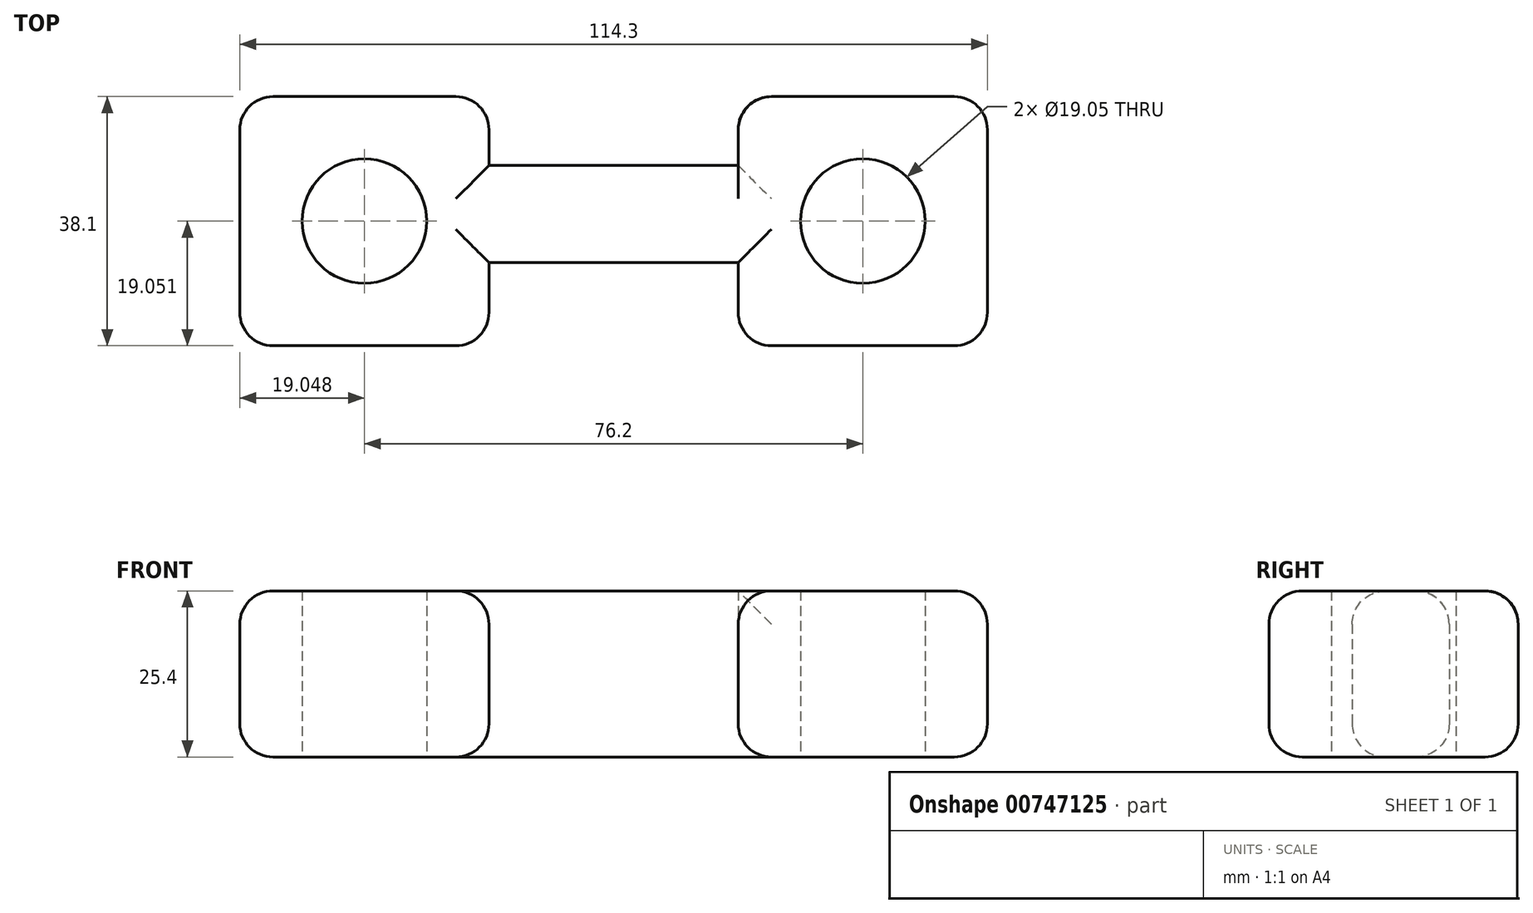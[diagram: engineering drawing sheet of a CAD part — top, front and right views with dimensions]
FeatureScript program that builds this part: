
annotation { "Feature Type Name" : "Feature", "Feature Type Description" : "" }
export const myFeature = defineFeature(function(context is Context, id is Id, definition is map)
    precondition{}
    {
        {
            var Q0;
            Q0=qCreatedBy(makeId("Top.planeOp"),FACE);
            var sketch = newSketch(context, id + "F0", { "sketchPlane" : qUnion([Q0])});
            skLineSegment(sketch, "E0.bottom", {"start": v(-66.91, 7.02) * mm, "end": v(-105.01, 7.02) * mm});
            skLineSegment(sketch, "E0.top", {"start": v(-66.91, 45.12) * mm, "end": v(-105.01, 45.12) * mm});
            skLineSegment(sketch, "E0.left", {"start": v(-66.91, 7.02) * mm, "end": v(-66.91, 45.12) * mm});
            skLineSegment(sketch, "E0.right", {"start": v(-105.01, 7.02) * mm, "end": v(-105.01, 45.12) * mm});
            skPoint(sketch, "E0.middle", {"position": v(-85.96, 26.07) * mm});
            skLineSegment(sketch, "E1.bottom", {"start": v(9.29, 7.02) * mm, "end": v(-28.81, 7.02) * mm});
            skLineSegment(sketch, "E1.top", {"start": v(9.29, 45.12) * mm, "end": v(-28.81, 45.12) * mm});
            skLineSegment(sketch, "E1.left", {"start": v(9.29, 7.02) * mm, "end": v(9.29, 45.12) * mm});
            skLineSegment(sketch, "E1.right", {"start": v(-28.81, 7.02) * mm, "end": v(-28.81, 45.12) * mm});
            skPoint(sketch, "E1.middle", {"position": v(-9.76, 26.07) * mm});
            skLineSegment(sketch, "E2.bottom", {"start": v(-28.81, 19.74) * mm, "end": v(-66.91, 19.74) * mm});
            skLineSegment(sketch, "E2.top", {"start": v(-28.81, 34.57) * mm, "end": v(-66.91, 34.57) * mm});
            skLineSegment(sketch, "E2.left", {"start": v(-28.81, 19.74) * mm, "end": v(-28.81, 34.57) * mm});
            skLineSegment(sketch, "E2.right", {"start": v(-66.91, 19.74) * mm, "end": v(-66.91, 34.57) * mm});
            skPoint(sketch, "E2.middle", {"position": v(-47.86, 27.16) * mm});
            skCircle(sketch, "E3", {"center": v(-85.96, 26.07) * mm, "radius": 9.53 * mm});
            skCircle(sketch, "E4", {"center": v(-9.76, 26.07) * mm, "radius": 9.53 * mm});
            skSolve(sketch);
        }
        {
            var Q0;
            {var subQ3=sQuery(id+"F0.wireOp",EDGE,"E0.bottom");Q0=makeQuery(id+"F0.imprint","IMPRINT",FACE,{"disambiguationData":[TD([[makeQuery(id+"F0.imprint","IMPRINT",EDGE,{"derivedFrom":subQ3}),-1.0]])]});}
            var Q1;
            Q1=makeQuery(id+"F0.imprint","IMPRINT",FACE,{"disambiguationData":[TD([[makeQuery(id+"F0.imprint","IMPRINT",EDGE,{"derivedFrom":sQuery(id+"F0.wireOp",EDGE,"E2.bottom")}),-1.0]])]});
            var Q2;
            {var subQ1=sQuery(id+"F0.wireOp",EDGE,"E1.bottom");Q2=makeQuery(id+"F0.imprint","IMPRINT",FACE,{"disambiguationData":[TD([[makeQuery(id+"F0.imprint","IMPRINT",EDGE,{"derivedFrom":subQ1}),-1.0]])]});}
            extrude(context, id + "F1", {"entities" : qUnion([Q0, Q1, Q2]), "depth" : 25.4 * mm, "offsetDistance" : 25.4 * mm});
        }
        {
            var Q0;
            Q0=makeQuery(id+"F1.opExtrude","CAP_EDGE",EDGE,{"disambiguationData":[OSD([sQuery(id+"F0.wireOp",EDGE,"E0.top")])],"isStart":false});
            var Q1;
            Q1=makeQuery(id+"F1.opExtrude","CAP_EDGE",EDGE,{"disambiguationData":[OSD([sQuery(id+"F0.wireOp",EDGE,"E0.top")])],"isStart":true});
            var Q2;
            Q2=makeQuery(id+"F1.opExtrude","SWEPT_EDGE",EDGE,{"disambiguationData":[OSD([sQuery(id+"F0.wireOp",EDGE,"E0.top"),sQuery(id+"F0.wireOp",EDGE,"E0.right")])]});
            var Q3;
            Q3=makeQuery(id+"F1.opExtrude","CAP_EDGE",EDGE,{"disambiguationData":[OSD([sQuery(id+"F0.wireOp",EDGE,"E0.right")])],"isStart":true});
            var Q4;
            Q4=makeQuery(id+"F1.opExtrude","CAP_EDGE",EDGE,{"disambiguationData":[OSD([sQuery(id+"F0.wireOp",EDGE,"E0.right")])],"isStart":false});
            var Q5;
            Q5=makeQuery(id+"F1.opExtrude","CAP_EDGE",EDGE,{"disambiguationData":[OSD([sQuery(id+"F0.wireOp",EDGE,"E0.bottom")])],"isStart":false});
            var Q6;
            Q6=makeQuery(id+"F1.opExtrude","CAP_EDGE",EDGE,{"disambiguationData":[OSD([sQuery(id+"F0.wireOp",EDGE,"E2.bottom")])],"isStart":false});
            var Q7;
            Q7=makeQuery(id+"F1.opExtrude","CAP_EDGE",EDGE,{"disambiguationData":[OSD([sQuery(id+"F0.wireOp",EDGE,"E2.top")])],"isStart":false});
            var Q8;
            {var subQ0=sQuery(id+"F0.wireOp",EDGE,"E0.left");Q8=makeQuery(id+"F1.opExtrude","CAP_EDGE",EDGE,{"disambiguationData":[OSD([subQ0]),TDD([makeQuery(id+"F0.imprint","IMPRINT",EDGE,{"disambiguationData":[TD([[makeQuery(id+"F0.imprint","INTERSECT",VERTEX,{"derivedFrom":[sQuery(id+"F0.wireOp",EDGE,"E0.top"),subQ0]}),1.0]])],"derivedFrom":subQ0})])],"isStart":false});}
            var Q9;
            {var subQ0=sQuery(id+"F0.wireOp",EDGE,"E0.left");Q9=makeQuery(id+"F1.opExtrude","CAP_EDGE",EDGE,{"disambiguationData":[OSD([subQ0]),TDD([makeQuery(id+"F0.imprint","IMPRINT",EDGE,{"disambiguationData":[TD([[makeQuery(id+"F0.imprint","INTERSECT",VERTEX,{"derivedFrom":[sQuery(id+"F0.wireOp",EDGE,"E0.bottom"),subQ0]}),-1.0]])],"derivedFrom":subQ0})])],"isStart":false});}
            var Q10;
            {var subQ0=sQuery(id+"F0.wireOp",EDGE,"E1.right");Q10=makeQuery(id+"F1.opExtrude","CAP_EDGE",EDGE,{"disambiguationData":[OSD([subQ0]),TDD([makeQuery(id+"F0.imprint","IMPRINT",EDGE,{"disambiguationData":[TD([[makeQuery(id+"F0.imprint","INTERSECT",VERTEX,{"derivedFrom":[sQuery(id+"F0.wireOp",EDGE,"E1.bottom"),subQ0]}),-1.0]])],"derivedFrom":subQ0})])],"isStart":false});}
            var Q11;
            Q11=makeQuery(id+"F1.opExtrude","CAP_EDGE",EDGE,{"disambiguationData":[OSD([sQuery(id+"F0.wireOp",EDGE,"E1.bottom")])],"isStart":false});
            var Q12;
            Q12=makeQuery(id+"F1.opExtrude","CAP_EDGE",EDGE,{"disambiguationData":[OSD([sQuery(id+"F0.wireOp",EDGE,"E1.left")])],"isStart":false});
            var Q13;
            Q13=makeQuery(id+"F1.opExtrude","CAP_EDGE",EDGE,{"disambiguationData":[OSD([sQuery(id+"F0.wireOp",EDGE,"E1.top")])],"isStart":false});
            var Q14;
            Q14=makeQuery(id+"F1.opExtrude","SWEPT_EDGE",EDGE,{"disambiguationData":[OSD([sQuery(id+"F0.wireOp",EDGE,"E1.bottom"),sQuery(id+"F0.wireOp",EDGE,"E1.left")])]});
            var Q15;
            Q15=makeQuery(id+"F1.opExtrude","SWEPT_EDGE",EDGE,{"disambiguationData":[OSD([sQuery(id+"F0.wireOp",EDGE,"E1.top"),sQuery(id+"F0.wireOp",EDGE,"E1.left")])]});
            var Q16;
            Q16=makeQuery(id+"F1.opExtrude","CAP_EDGE",EDGE,{"disambiguationData":[OSD([sQuery(id+"F0.wireOp",EDGE,"E1.left")])],"isStart":true});
            var Q17;
            Q17=makeQuery(id+"F1.opExtrude","CAP_EDGE",EDGE,{"disambiguationData":[OSD([sQuery(id+"F0.wireOp",EDGE,"E2.bottom")])],"isStart":true});
            var Q18;
            {var subQ0=sQuery(id+"F0.wireOp",EDGE,"E0.left");Q18=makeQuery(id+"F1.opExtrude","CAP_EDGE",EDGE,{"disambiguationData":[OSD([subQ0]),TDD([makeQuery(id+"F0.imprint","IMPRINT",EDGE,{"disambiguationData":[TD([[makeQuery(id+"F0.imprint","INTERSECT",VERTEX,{"derivedFrom":[sQuery(id+"F0.wireOp",EDGE,"E0.bottom"),subQ0]}),-1.0]])],"derivedFrom":subQ0})])],"isStart":true});}
            var Q19;
            Q19=makeQuery(id+"F1.opExtrude","SWEPT_EDGE",EDGE,{"disambiguationData":[OSD([sQuery(id+"F0.wireOp",EDGE,"E0.bottom"),sQuery(id+"F0.wireOp",EDGE,"E0.left")])]});
            var Q20;
            Q20=makeQuery(id+"F1.opExtrude","SWEPT_EDGE",EDGE,{"disambiguationData":[OSD([sQuery(id+"F0.wireOp",EDGE,"E1.bottom"),sQuery(id+"F0.wireOp",EDGE,"E1.right")])]});
            var Q21;
            Q21=makeQuery(id+"F1.opExtrude","CAP_EDGE",EDGE,{"disambiguationData":[OSD([sQuery(id+"F0.wireOp",EDGE,"E0.bottom")])],"isStart":true});
            var Q22;
            Q22=makeQuery(id+"F1.opExtrude","CAP_EDGE",EDGE,{"disambiguationData":[OSD([sQuery(id+"F0.wireOp",EDGE,"E2.top")])],"isStart":true});
            var Q23;
            Q23=makeQuery(id+"F1.opExtrude","CAP_EDGE",EDGE,{"disambiguationData":[OSD([sQuery(id+"F0.wireOp",EDGE,"E1.top")])],"isStart":true});
            var Q24;
            Q24=makeQuery(id+"F1.opExtrude","SWEPT_EDGE",EDGE,{"disambiguationData":[OSD([sQuery(id+"F0.wireOp",EDGE,"E1.top"),sQuery(id+"F0.wireOp",EDGE,"E1.right")])]});
            var Q25;
            {var subQ0=sQuery(id+"F0.wireOp",EDGE,"E1.right");Q25=makeQuery(id+"F1.opExtrude","CAP_EDGE",EDGE,{"disambiguationData":[OSD([subQ0]),TDD([makeQuery(id+"F0.imprint","IMPRINT",EDGE,{"disambiguationData":[TD([[makeQuery(id+"F0.imprint","INTERSECT",VERTEX,{"derivedFrom":[sQuery(id+"F0.wireOp",EDGE,"E1.top"),subQ0]}),1.0]])],"derivedFrom":subQ0})])],"isStart":true});}
            var Q26;
            {var subQ0=sQuery(id+"F0.wireOp",EDGE,"E0.left");Q26=makeQuery(id+"F1.opExtrude","CAP_EDGE",EDGE,{"disambiguationData":[OSD([subQ0]),TDD([makeQuery(id+"F0.imprint","IMPRINT",EDGE,{"disambiguationData":[TD([[makeQuery(id+"F0.imprint","INTERSECT",VERTEX,{"derivedFrom":[sQuery(id+"F0.wireOp",EDGE,"E0.top"),subQ0]}),1.0]])],"derivedFrom":subQ0})])],"isStart":true});}
            var Q27;
            Q27=makeQuery(id+"F1.opExtrude","CAP_EDGE",EDGE,{"disambiguationData":[OSD([sQuery(id+"F0.wireOp",EDGE,"E1.bottom")])],"isStart":true});
            var Q28;
            {var subQ0=sQuery(id+"F0.wireOp",EDGE,"E1.right");Q28=makeQuery(id+"F1.opExtrude","CAP_EDGE",EDGE,{"disambiguationData":[OSD([subQ0]),TDD([makeQuery(id+"F0.imprint","IMPRINT",EDGE,{"disambiguationData":[TD([[makeQuery(id+"F0.imprint","INTERSECT",VERTEX,{"derivedFrom":[sQuery(id+"F0.wireOp",EDGE,"E1.bottom"),subQ0]}),-1.0]])],"derivedFrom":subQ0})])],"isStart":true});}
            fillet(context, id + "F2", {"entities" : qUnion([Q0, Q1, Q2, Q3, Q4, Q5, Q6, Q7, Q8, Q9, Q10, Q11, Q12, Q13, Q14, Q15, Q16, Q17, Q18, Q19, Q20, Q21, Q22, Q23, Q24, Q25, Q26, Q27, Q28]), "radius" : 5.08 * mm, "tangentPropagation" : true, "allowEdgeOverflow" : false});
        }
        {
            var Q0;
            Q0=makeQuery(id+"F1.opExtrude","SWEPT_EDGE",EDGE,{"disambiguationData":[OSD([sQuery(id+"F0.wireOp",EDGE,"E0.top"),sQuery(id+"F0.wireOp",EDGE,"E0.left")])]});
            var Q1;
            Q1=makeQuery(id+"F1.opExtrude","SWEPT_EDGE",EDGE,{"disambiguationData":[OSD([sQuery(id+"F0.wireOp",EDGE,"E0.bottom"),sQuery(id+"F0.wireOp",EDGE,"E0.right")])]});
            fillet(context, id + "F3", {"entities" : qUnion([Q0, Q1]), "radius" : 5.08 * mm, "tangentPropagation" : true, "allowEdgeOverflow" : false});
        }
    });
